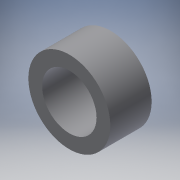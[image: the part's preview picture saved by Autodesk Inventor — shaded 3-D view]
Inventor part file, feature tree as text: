
AUTODESK INVENTOR PART (.ipt)
format: ipt  version: 2019 (Build 230136000, 136)  size: 100,352 bytes
history: native  units: in
note: dims shown in document units (in); Inventor stores cm internally (conversion verified against a paired STEP export)
features: other x2, extrude x1, sketch x1, reference x1
ambient origin geometry x8: Origin, YZ Plane, XZ Plane, XY Plane, X Axis, Y Axis, Z Axis, Center Point
bodies: Solid1 (feature_tree)
feature tree (5):
  extrude  "Extrusion1"  Depth=3.25in TaperAngle=0.0deg
  sketch  "Sketch1"  dims[d0=1.0in d1=3.25in d2=0.0in]
  reference  "Reference1"
  other  "Assembly1"
  other  "Wheel_Rim:1"
